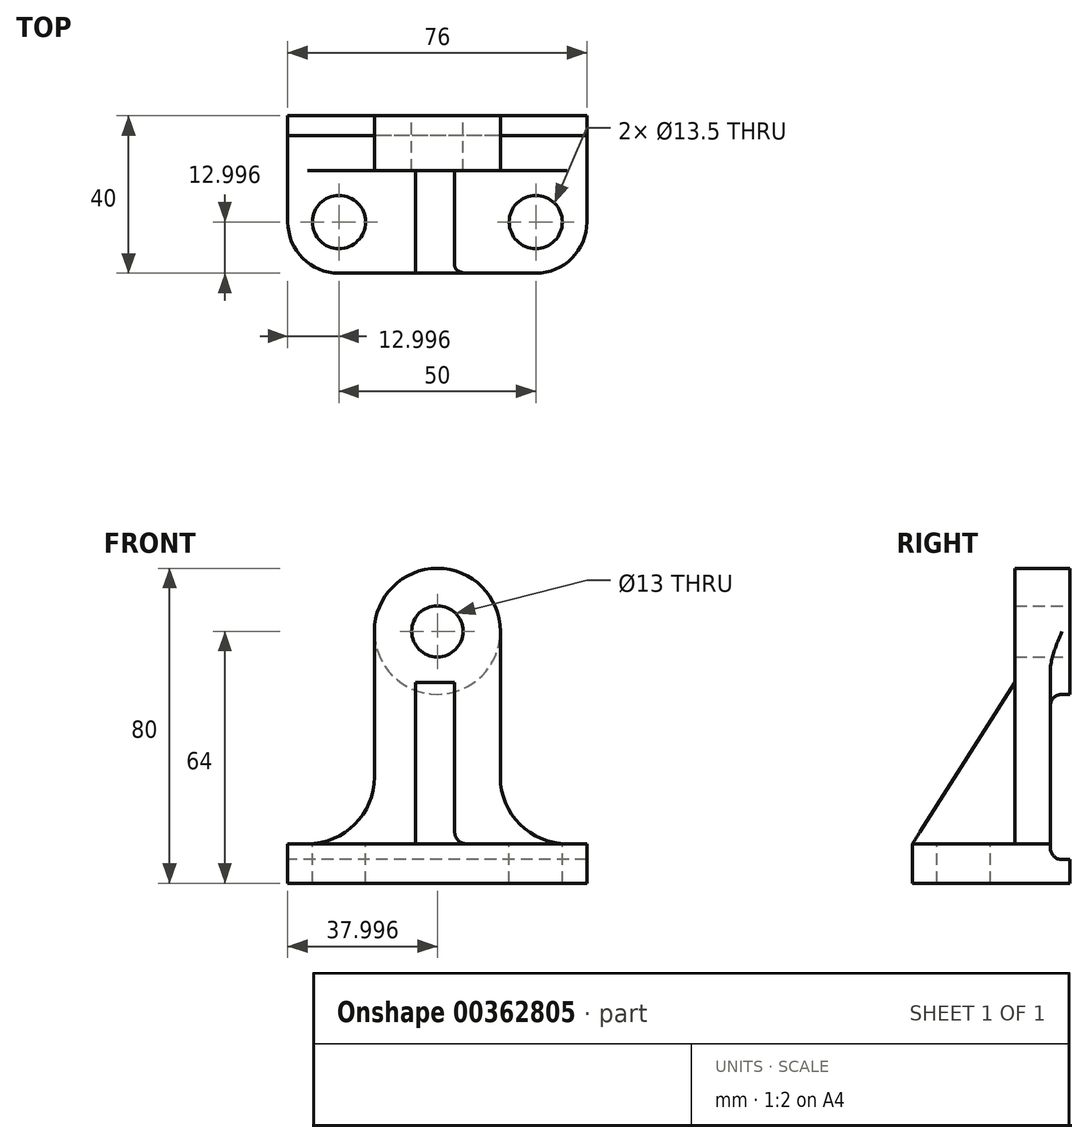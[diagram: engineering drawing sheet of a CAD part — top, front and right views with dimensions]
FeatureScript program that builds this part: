
annotation { "Feature Type Name" : "Feature", "Feature Type Description" : "" }
export const myFeature = defineFeature(function(context is Context, id is Id, definition is map)
    precondition{}
    {
        {
            var Q0;
            Q0=qCreatedBy(makeId("Top.planeOp"),FACE);
            var sketch = newSketch(context, id + "F0", { "sketchPlane" : qUnion([Q0])});
            skLineSegment(sketch, "E0.bottom", {"start": v(-37.4, 19.69) * mm, "end": v(38.6, 19.69) * mm});
            skLineSegment(sketch, "E0.top", {"start": v(-37.4, -20.31) * mm, "end": v(38.6, -20.31) * mm});
            skLineSegment(sketch, "E0.left", {"start": v(-37.4, 19.69) * mm, "end": v(-37.4, -20.31) * mm});
            skLineSegment(sketch, "E0.right", {"start": v(38.6, 19.69) * mm, "end": v(38.6, -20.31) * mm});
            skLineSegment(sketch, "E1", {"start": v(-37.4, 19.69) * mm, "end": v(38.6, -20.31) * mm, "construction": true});
            skSolve(sketch);
        }
        {
            var Q0;
            Q0 = qSketchRegion(id + "F0", true);
            extrude(context, id + "F1", {"entities" : qUnion([Q0]), "depth" : 10 * mm});
        }
        {
            var Q0;
            Q0=makeQuery(id+"F1.opExtrude","SWEPT_EDGE",EDGE,{"disambiguationData":[OSD([sQuery(id+"F0.wireOp",EDGE,"E0.top"),sQuery(id+"F0.wireOp",EDGE,"E0.left")])]});
            var Q1;
            Q1=makeQuery(id+"F1.opExtrude","SWEPT_EDGE",EDGE,{"disambiguationData":[OSD([sQuery(id+"F0.wireOp",EDGE,"E0.top"),sQuery(id+"F0.wireOp",EDGE,"E0.right")])]});
            fillet(context, id + "F2", {"entities" : qUnion([Q0, Q1]), "radius" : 13 * mm, "tangentPropagation" : true, "allowEdgeOverflow" : false});
        }
        {
            var Q0;
            Q0=makeQuery(id+"F1.opExtrude","CAP_FACE",FACE,{"disambiguationData":[OSD([sQuery(id+"F0.wireOp",EDGE,"E0.bottom"),sQuery(id+"F0.wireOp",EDGE,"E0.top"),sQuery(id+"F0.wireOp",EDGE,"E0.left"),sQuery(id+"F0.wireOp",EDGE,"E0.right")])],"isStart":false});
            var sketch = newSketch(context, id + "F3", { "sketchPlane" : qUnion([Q0])});
            skPoint(sketch, "E2", {"position": v(-24.4, -7.31) * mm});
            skPoint(sketch, "E3", {"position": v(25.6, -7.31) * mm});
            skSolve(sketch);
        }
        {
            var Q0;
            Q0=sQuery(id+"F3.wireOp",VERTEX,"E2");
            var Q1;
            Q1=sQuery(id+"F3.wireOp",VERTEX,"E3");
            var Q2;
            Q2=makeQuery(id+"F1.opExtrude","SWEPT_BODY",BODY,{"disambiguationData":[OSD([sQuery(id+"F0.wireOp",EDGE,"E0.bottom"),sQuery(id+"F0.wireOp",EDGE,"E0.top"),sQuery(id+"F0.wireOp",EDGE,"E0.left"),sQuery(id+"F0.wireOp",EDGE,"E0.right")])]});
            hole(context, id + "F4", {"style" : HoleStyle.SIMPLE, "endStyle" : HoleEndStyle.THROUGH, "holeDiameter" : 13.5 * mm, "isTappedThrough" : true, "tappedDepth" : 12 * mm, "tapClearance" : 3, "locations" : qUnion([Q0, Q1]), "scope" : qUnion([Q2])});
        }
        {
            var Q0;
            Q0=makeQuery(id+"F1.opExtrude","SWEPT_FACE",FACE,{"disambiguationData":[OSD([sQuery(id+"F0.wireOp",EDGE,"E0.bottom")])]});
            var sketch = newSketch(context, id + "F5", { "sketchPlane" : qUnion([Q0])});
            skLineSegment(sketch, "E4.0", {"start": v(32.4, 10) * mm, "end": v(-33.6, 10) * mm});
            skLineSegment(sketch, "E5", {"start": v(15.4, 27) * mm, "end": v(15.4, 64) * mm});
            skArc(sketch, "E6", {"start": v(15.4, 64) * mm, "mid": v(-0.6, 80) * mm, "end": v(-16.6, 64) * mm});
            skLineSegment(sketch, "E7", {"start": v(-16.6, 64) * mm, "end": v(-16.6, 27) * mm});
            skLineSegment(sketch, "E8", {"start": v(-0.6, 64) * mm, "end": v(-0.6, 10) * mm, "construction": true});
            skArc(sketch, "E9", {"start": v(15.4, 27) * mm, "mid": v(20.38, 14.98) * mm, "end": v(32.4, 10) * mm});
            skArc(sketch, "E10", {"start": v(-33.6, 10) * mm, "mid": v(-21.57, 14.98) * mm, "end": v(-16.6, 27) * mm});
            skPoint(sketch, "E11.orphan", {"position": v(-38.6, 10) * mm});
            skPoint(sketch, "E12.orphan", {"position": v(37.4, 10) * mm});
            skSolve(sketch);
        }
        {
            var Q0;
            Q0 = qSketchRegion(id + "F5", true);
            extrude(context, id + "F6", {"entities" : qUnion([Q0]), "operationType" : NewBodyOperationType.ADD, "oppositeDirection" : true, "depth" : 14 * mm});
        }
        {
            var Q0;
            Q0=qCreatedBy(makeId("Right.planeOp"),FACE);
            var sketch = newSketch(context, id + "F7", { "sketchPlane" : qUnion([Q0])});
            skLineSegment(sketch, "E13", {"start": v(5.69, 10) * mm, "end": v(5.69, 51) * mm});
            skLineSegment(sketch, "E14", {"start": v(5.69, 10) * mm, "end": v(-20.31, 10) * mm});
            skLineSegment(sketch, "E15", {"start": v(-20.31, 10) * mm, "end": v(5.69, 51) * mm});
            skPoint(sketch, "E16.orphan", {"position": v(5.69, 79.99) * mm});
            skSolve(sketch);
        }
        {
            var Q0;
            Q0 = qSketchRegion(id + "F7", true);
            extrude(context, id + "F8", {"entities" : qUnion([Q0]), "operationType" : NewBodyOperationType.ADD, "depth" : 5 * mm, "hasSecondDirection" : true, "secondDirectionOppositeDirection" : true, "secondDirectionDepth" : 5 * mm});
        }
        {
            var Q0;
            Q0=makeQuery(id+"F6.boolean.opBoolean","MERGE",FACE,{"derivedFrom":[makeQuery(id+"F1.opExtrude","SWEPT_FACE",FACE,{"disambiguationData":[OSD([sQuery(id+"F0.wireOp",EDGE,"E0.bottom")])]}),makeQuery(id+"F6.opExtrude","CAP_FACE",FACE,{"disambiguationData":[OSD([sQuery(id+"F5.wireOp",EDGE,"E4.0"),sQuery(id+"F5.wireOp",EDGE,"E5"),sQuery(id+"F5.wireOp",EDGE,"E6"),sQuery(id+"F5.wireOp",EDGE,"E7"),sQuery(id+"F5.wireOp",EDGE,"E9"),sQuery(id+"F5.wireOp",EDGE,"E10")])],"isStart":true})]});
            var sketch = newSketch(context, id + "F9", { "sketchPlane" : qUnion([Q0])});
            skLineSegment(sketch, "E17", {"start": v(-38.6, 6) * mm, "end": v(37.4, 6) * mm});
            skLineSegment(sketch, "E18.0.1", {"start": v(37.4, 6) * mm, "end": v(37.4, 10) * mm});
            skLineSegment(sketch, "E18.0.2", {"start": v(37.4, 10) * mm, "end": v(32.4, 10) * mm});
            skArc(sketch, "E18.0.3", {"start": v(32.4, 10) * mm, "mid": v(20.38, 14.98) * mm, "end": v(15.4, 27) * mm});
            skLineSegment(sketch, "E18.0.4", {"start": v(15.4, 27) * mm, "end": v(15.4, 64) * mm});
            skLineSegment(sketch, "E18.0.6", {"start": v(-16.6, 64) * mm, "end": v(-16.6, 27) * mm});
            skArc(sketch, "E18.0.7", {"start": v(-16.6, 27) * mm, "mid": v(-21.57, 14.98) * mm, "end": v(-33.6, 10) * mm});
            skLineSegment(sketch, "E18.0.8", {"start": v(-33.6, 10) * mm, "end": v(-38.6, 10) * mm});
            skLineSegment(sketch, "E18.0.9", {"start": v(-38.6, 10) * mm, "end": v(-38.6, 6) * mm});
            skArc(sketch, "E19", {"start": v(-16.6, 64) * mm, "mid": v(-0.6, 48) * mm, "end": v(15.4, 64) * mm});
            skSolve(sketch);
        }
        {
            var Q0;
            Q0 = qSketchRegion(id + "F9", true);
            extrude(context, id + "F10", {"entities" : qUnion([Q0]), "operationType" : NewBodyOperationType.REMOVE, "oppositeDirection" : true, "depth" : 5 * mm});
        }
        {
            var Q0;
            Q0=makeQuery(id+"F10.boolean.opBoolean","COPY",EDGE,{"derivedFrom":makeQuery(id+"F10.opExtrude","CAP_EDGE",EDGE,{"disambiguationData":[OSD([sQuery(id+"F9.wireOp",EDGE,"E17")])],"isStart":false})});
            var Q1;
            Q1=makeQuery(id+"F10.boolean.opBoolean","COPY",EDGE,{"derivedFrom":makeQuery(id+"F10.opExtrude","CAP_EDGE",EDGE,{"disambiguationData":[OSD([sQuery(id+"F9.wireOp",EDGE,"E19")])],"isStart":false})});
            var Q2;
            {var subQ0=sQuery(id+"F5.wireOp",EDGE,"E10");var subQ1=sQuery(id+"F5.wireOp",EDGE,"E4.0");Q2=makeQuery(id+"F8.boolean.opBoolean","SPLIT",EDGE,{"disambiguationData":[TD([makeQuery(id+"F6.opExtrude","SWEPT_FACE",FACE,{"disambiguationData":[OSD([subQ0])]})])],"derivedFrom":makeQuery(id+"F6.opExtrude","CAP_EDGE",EDGE,{"disambiguationData":[OSD([subQ1])],"isStart":false})});}
            var Q3;
            Q3=makeQuery(id+"F8.opExtrude","CAP_EDGE",EDGE,{"disambiguationData":[OSD([sQuery(id+"F7.wireOp",EDGE,"E14")])],"isStart":false});
            var Q4;
            Q4=makeQuery(id+"F8.opExtrude","CAP_EDGE",EDGE,{"disambiguationData":[OSD([sQuery(id+"F7.wireOp",EDGE,"E14")])],"isStart":true});
            var Q5;
            {var subQ0=sQuery(id+"F5.wireOp",EDGE,"E9");var subQ1=sQuery(id+"F5.wireOp",EDGE,"E4.0");Q5=makeQuery(id+"F8.boolean.opBoolean","SPLIT",EDGE,{"disambiguationData":[TD([makeQuery(id+"F6.opExtrude","SWEPT_FACE",FACE,{"disambiguationData":[OSD([subQ0])]})])],"derivedFrom":makeQuery(id+"F6.opExtrude","CAP_EDGE",EDGE,{"disambiguationData":[OSD([subQ1])],"isStart":false})});}
            var Q6;
            Q6=makeQuery(id+"F8.opExtrude","CAP_EDGE",EDGE,{"disambiguationData":[OSD([sQuery(id+"F7.wireOp",EDGE,"E13")])],"isStart":false});
            var Q7;
            Q7=makeQuery(id+"F8.opExtrude","CAP_EDGE",EDGE,{"disambiguationData":[OSD([sQuery(id+"F7.wireOp",EDGE,"E13")])],"isStart":true});
            fillet(context, id + "F11", {"entities" : qUnion([Q0, Q1, Q2, Q3, Q4, Q5, Q6, Q7]), "radius" : 3 * mm, "tangentPropagation" : true, "allowEdgeOverflow" : false});
        }
        {
            var Q0;
            {var subQ0=sQuery(id+"F5.wireOp",EDGE,"E6");Q0=makeQuery(id+"F10.boolean.opBoolean","SPLIT",FACE,{"disambiguationData":[TD([makeQuery(id+"F6.opExtrude","SWEPT_FACE",FACE,{"disambiguationData":[OSD([subQ0])]})])],"derivedFrom":makeQuery(id+"F6.boolean.opBoolean","MERGE",FACE,{"derivedFrom":[makeQuery(id+"F1.opExtrude","SWEPT_FACE",FACE,{"disambiguationData":[OSD([sQuery(id+"F0.wireOp",EDGE,"E0.bottom")])]}),makeQuery(id+"F6.opExtrude","CAP_FACE",FACE,{"disambiguationData":[OSD([sQuery(id+"F5.wireOp",EDGE,"E4.0"),sQuery(id+"F5.wireOp",EDGE,"E5"),subQ0,sQuery(id+"F5.wireOp",EDGE,"E7"),sQuery(id+"F5.wireOp",EDGE,"E9"),sQuery(id+"F5.wireOp",EDGE,"E10")])],"isStart":true})]})});}
            var sketch = newSketch(context, id + "F12", { "sketchPlane" : qUnion([Q0])});
            skPoint(sketch, "E20", {"position": v(-0.6, 64) * mm});
            skSolve(sketch);
        }
        {
            var Q0;
            Q0=sQuery(id+"F12.wireOp",VERTEX,"E20");
            var Q1;
            Q1=makeQuery(id+"F1.opExtrude","SWEPT_BODY",BODY,{"disambiguationData":[OSD([sQuery(id+"F0.wireOp",EDGE,"E0.bottom"),sQuery(id+"F0.wireOp",EDGE,"E0.top"),sQuery(id+"F0.wireOp",EDGE,"E0.left"),sQuery(id+"F0.wireOp",EDGE,"E0.right")])]});
            hole(context, id + "F13", {"style" : HoleStyle.SIMPLE, "endStyle" : HoleEndStyle.THROUGH, "holeDiameter" : 13 * mm, "isTappedThrough" : true, "tappedDepth" : 12 * mm, "tapClearance" : 3, "locations" : qUnion([Q0]), "scope" : qUnion([Q1])});
        }
    });
